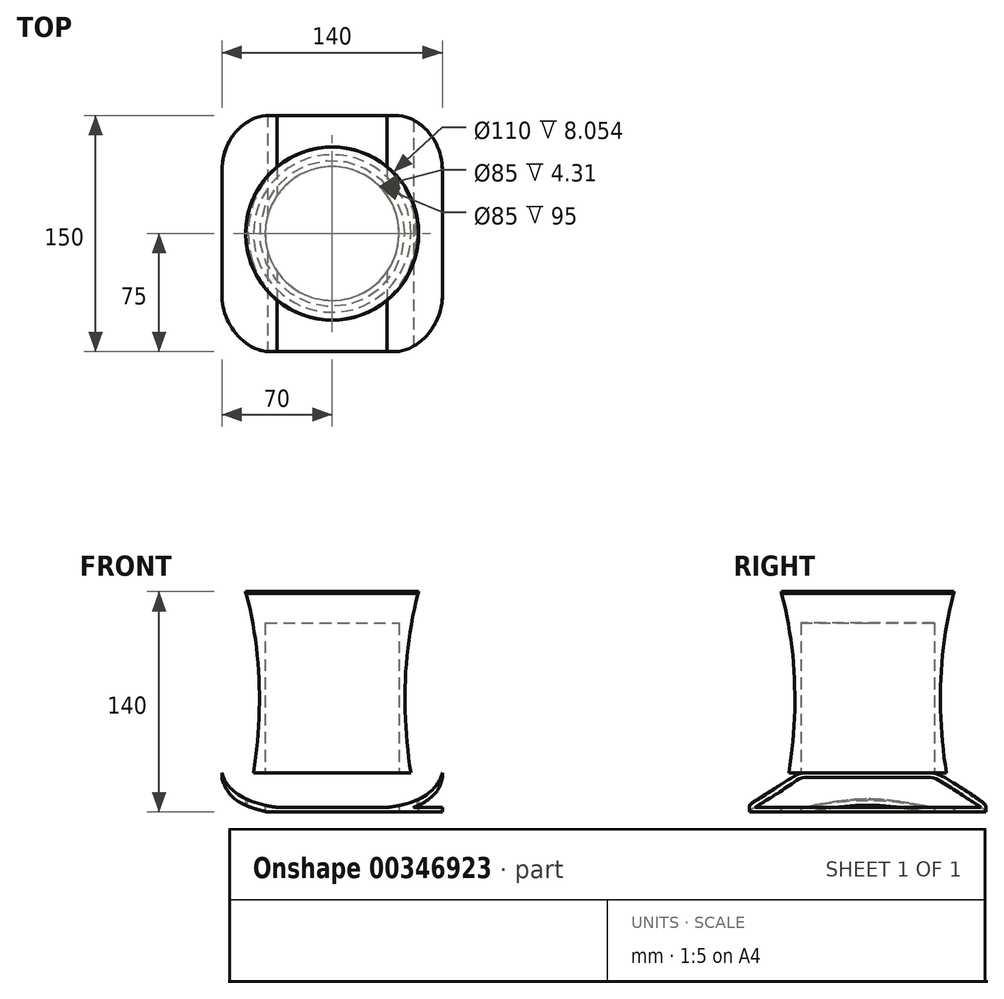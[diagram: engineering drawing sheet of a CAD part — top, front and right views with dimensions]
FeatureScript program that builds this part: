
annotation { "Feature Type Name" : "Feature", "Feature Type Description" : "" }
export const myFeature = defineFeature(function(context is Context, id is Id, definition is map)
    precondition{}
    {
        {
            var Q0;
            Q0=qCreatedBy(makeId("Top.planeOp"),FACE);
            var sketch = newSketch(context, id + "F0", { "sketchPlane" : qUnion([Q0])});
            skCircle(sketch, "E0", {"center": v(0, 0) * mm, "radius": 55 * mm});
            skSolve(sketch);
        }
        {
            var Q0;
            Q0=makeQuery(id+"F0.imprint","IMPRINT",FACE,{"disambiguationData":[TD([[makeQuery(id+"F0.imprint","IMPRINT",EDGE,{"derivedFrom":sQuery(id+"F0.wireOp",EDGE,"E0")}),1.0]])]});
            extrude(context, id + "F1", {"entities" : qUnion([Q0]), "depth" : 140 * mm});
        }
        {
            var Q0;
            Q0=makeQuery(id+"F1.opExtrude","CAP_FACE",FACE,{"disambiguationData":[OSD([sQuery(id+"F0.wireOp",EDGE,"E0")])],"isStart":true});
            var sketch = newSketch(context, id + "F2", { "sketchPlane" : qUnion([Q0])});
            skCircle(sketch, "E1", {"center": v(0, 0) * mm, "radius": 42.5 * mm});
            skSolve(sketch);
        }
        {
            var Q0;
            Q0=makeQuery(id+"F2.imprint","IMPRINT",FACE,{"disambiguationData":[TD([[makeQuery(id+"F2.imprint","IMPRINT",EDGE,{"derivedFrom":sQuery(id+"F2.wireOp",EDGE,"E1")}),1.0]])]});
            extrude(context, id + "F3", {"entities" : qUnion([Q0]), "operationType" : NewBodyOperationType.REMOVE, "oppositeDirection" : true, "depth" : 120 * mm});
        }
        {
            var Q0;
            Q0=qCreatedBy(makeId("Front.planeOp"),FACE);
            var sketch = newSketch(context, id + "F4", { "sketchPlane" : qUnion([Q0])});
            skFitSpline(sketch, "E2", {"points": [v(-54.88, 139.91) * mm, v(-55.14, 0) * mm], "startDerivative": vector(37.45, -140.44) * mm, "endDerivative": vector(-32.77, -131.05) * mm});
            skLineSegment(sketch, "E3", {"start": v(-54.88, 139.91) * mm, "end": v(-55.14, 0) * mm});
            skSolve(sketch);
        }
        {
            var Q0;
            Q0=makeQuery(id+"F4.imprint","IMPRINT",FACE,{"disambiguationData":[TD([[makeQuery(id+"F4.imprint","IMPRINT",EDGE,{"derivedFrom":sQuery(id+"F4.wireOp",EDGE,"E2")}),-1.0]])]});
            var Q1;
            Q1=makeQuery(id+"F1.opExtrude","CAP_EDGE",EDGE,{"disambiguationData":[OSD([sQuery(id+"F0.wireOp",EDGE,"E0")])],"isStart":true});
            revolve(context, id + "F5", {"operationType" : NewBodyOperationType.REMOVE, "entities" : qUnion([Q0]), "axis" : qUnion([Q1]), "revolveType" : RevolveType.FULL, "oppositeDirection" : true});
        }
        {
            var Q0;
            Q0=qCreatedBy(makeId("Front.planeOp"),FACE);
            var sketch = newSketch(context, id + "F6", { "sketchPlane" : qUnion([Q0])});
            skLineSegment(sketch, "E4.bottom", {"start": v(-55.94, 142.28) * mm, "end": v(-54.88, 142.28) * mm});
            skLineSegment(sketch, "E4.top", {"start": v(-55.94, 72.28) * mm, "end": v(-54.88, 72.28) * mm});
            skLineSegment(sketch, "E4.left", {"start": v(-55.94, 142.28) * mm, "end": v(-55.94, 72.28) * mm});
            skLineSegment(sketch, "E4.right", {"start": v(-54.88, 142.28) * mm, "end": v(-54.88, 72.28) * mm});
            skSolve(sketch);
        }
        {
            var Q0;
            Q0=makeQuery(id+"F6.imprint","IMPRINT",FACE,{"disambiguationData":[TD([[makeQuery(id+"F6.imprint","IMPRINT",EDGE,{"derivedFrom":sQuery(id+"F6.wireOp",EDGE,"E4.bottom")}),-1.0]])]});
            var Q1;
            Q1=makeQuery(id+"F1.opExtrude","CAP_EDGE",EDGE,{"disambiguationData":[OSD([sQuery(id+"F0.wireOp",EDGE,"E0")])],"isStart":false});
            revolve(context, id + "F7", {"operationType" : NewBodyOperationType.REMOVE, "entities" : qUnion([Q0]), "axis" : qUnion([Q1]), "revolveType" : RevolveType.FULL, "oppositeDirection" : true});
        }
        {
            var Q0;
            Q0=qCreatedBy(makeId("Top.planeOp"),FACE);
            var sketch = newSketch(context, id + "F8", { "sketchPlane" : qUnion([Q0])});
            skCircle(sketch, "E5", {"center": v(0, 0) * mm, "radius": 55 * mm});
            skLineSegment(sketch, "E6.bottom", {"start": v(0, 0) * mm, "end": v(70, 0) * mm});
            skLineSegment(sketch, "E6.top", {"start": v(0, 75) * mm, "end": v(70, 75) * mm});
            skLineSegment(sketch, "E6.left", {"start": v(0, 0) * mm, "end": v(0, 75) * mm});
            skLineSegment(sketch, "E6.right", {"start": v(70, 0) * mm, "end": v(70, 75) * mm});
            skLineSegment(sketch, "E7.bottom", {"start": v(0, 0) * mm, "end": v(-70, 0) * mm});
            skLineSegment(sketch, "E7.top", {"start": v(0, 75) * mm, "end": v(-70, 75) * mm});
            skLineSegment(sketch, "E7.right", {"start": v(-70, 0) * mm, "end": v(-70, 75) * mm});
            skLineSegment(sketch, "E8.top", {"start": v(0, -75) * mm, "end": v(70, -75) * mm});
            skLineSegment(sketch, "E8.left", {"start": v(0, 0) * mm, "end": v(0, -75) * mm});
            skLineSegment(sketch, "E8.right", {"start": v(70, 0) * mm, "end": v(70, -75) * mm});
            skLineSegment(sketch, "E9.top", {"start": v(0, -75) * mm, "end": v(-70, -75) * mm});
            skLineSegment(sketch, "E9.right", {"start": v(-70, 0) * mm, "end": v(-70, -75) * mm});
            skSolve(sketch);
        }
        {
            var Q0;
            {var subQ0=sQuery(id+"F8.wireOp",EDGE,"E8.top");Q0=makeQuery(id+"F8.imprint","IMPRINT",FACE,{"disambiguationData":[TD([[makeQuery(id+"F8.imprint","IMPRINT",EDGE,{"derivedFrom":subQ0}),1.0]])]});}
            var Q1;
            {var subQ1=sQuery(id+"F8.wireOp",EDGE,"E6.top");Q1=makeQuery(id+"F8.imprint","IMPRINT",FACE,{"disambiguationData":[TD([[makeQuery(id+"F8.imprint","IMPRINT",EDGE,{"derivedFrom":subQ1}),-1.0]])]});}
            var Q2;
            {var subQ1=sQuery(id+"F8.wireOp",EDGE,"E9.top");Q2=makeQuery(id+"F8.imprint","IMPRINT",FACE,{"disambiguationData":[TD([[makeQuery(id+"F8.imprint","IMPRINT",EDGE,{"derivedFrom":subQ1}),-1.0]])]});}
            var Q3;
            {var subQ2=sQuery(id+"F8.wireOp",EDGE,"E7.top");Q3=makeQuery(id+"F8.imprint","IMPRINT",FACE,{"disambiguationData":[TD([[makeQuery(id+"F8.imprint","IMPRINT",EDGE,{"derivedFrom":subQ2}),1.0]])]});}
            extrude(context, id + "F9", {"entities" : qUnion([Q0, Q1, Q2, Q3]), "operationType" : NewBodyOperationType.ADD, "depth" : 25 * mm});
        }
        {
            var Q0;
            Q0=makeQuery(id+"F9.opExtrude","CAP_FACE",FACE,{"disambiguationData":[OSD([sQuery(id+"F8.wireOp",EDGE,"E5"),sQuery(id+"F8.wireOp",EDGE,"E6.top"),sQuery(id+"F8.wireOp",EDGE,"E6.right"),sQuery(id+"F8.wireOp",EDGE,"E7.top"),sQuery(id+"F8.wireOp",EDGE,"E7.right"),sQuery(id+"F8.wireOp",EDGE,"E8.top"),sQuery(id+"F8.wireOp",EDGE,"E8.right"),sQuery(id+"F8.wireOp",EDGE,"E9.top"),sQuery(id+"F8.wireOp",EDGE,"E9.right")])],"isStart":false});
            var sketch = newSketch(context, id + "F10", { "sketchPlane" : qUnion([Q0])});
            skLineSegment(sketch, "E10", {"start": v(-70, 75) * mm, "end": v(-40, 75) * mm});
            skLineSegment(sketch, "E11", {"start": v(-70, 75) * mm, "end": v(-70, 40) * mm});
            skPoint(sketch, "E12", {"position": v(-70, 57.5) * mm});
            skFitSpline(sketch, "E13", {"points": [v(-40, 75) * mm, v(-70, 40) * mm], "startDerivative": vector(-45, 0) * mm, "endDerivative": vector(0, -61.02) * mm});
            skLineSegment(sketch, "E14", {"start": v(70, 75) * mm, "end": v(40, 75) * mm});
            skLineSegment(sketch, "E15", {"start": v(70, 75) * mm, "end": v(70, 40) * mm});
            skLineSegment(sketch, "E16", {"start": v(-70, -40) * mm, "end": v(-70, -75) * mm});
            skLineSegment(sketch, "E17", {"start": v(-70, -75) * mm, "end": v(-40, -75) * mm});
            skFitSpline(sketch, "E18", {"points": [v(-70, -40) * mm, v(-40, -75) * mm], "startDerivative": vector(0, -52.5) * mm, "endDerivative": vector(45, 0) * mm});
            skFitSpline(sketch, "E19", {"points": [v(40, 75) * mm, v(70, 40) * mm], "startDerivative": vector(45, 0) * mm, "endDerivative": vector(0, -60.24) * mm});
            skLineSegment(sketch, "E20", {"start": v(40, -75) * mm, "end": v(70, -75) * mm});
            skLineSegment(sketch, "E21", {"start": v(70, -75) * mm, "end": v(70, -40) * mm});
            skFitSpline(sketch, "E22", {"points": [v(40, -75) * mm, v(70, -40) * mm], "startDerivative": vector(45, 0) * mm, "endDerivative": vector(0, 52.5) * mm});
            skSolve(sketch);
        }
        {
            var Q0;
            Q0=makeQuery(id+"F10.imprint","IMPRINT",FACE,{"disambiguationData":[TD([[makeQuery(id+"F10.imprint","IMPRINT",EDGE,{"derivedFrom":sQuery(id+"F10.wireOp",EDGE,"E10")}),-1.0]])]});
            var Q1;
            Q1=makeQuery(id+"F10.imprint","IMPRINT",FACE,{"disambiguationData":[TD([[makeQuery(id+"F10.imprint","IMPRINT",EDGE,{"derivedFrom":sQuery(id+"F10.wireOp",EDGE,"E14")}),-1.0]])]});
            var Q2;
            Q2=makeQuery(id+"F10.imprint","IMPRINT",FACE,{"disambiguationData":[TD([[makeQuery(id+"F10.imprint","IMPRINT",EDGE,{"derivedFrom":sQuery(id+"F10.wireOp",EDGE,"E20")}),1.0]])]});
            var Q3;
            Q3=makeQuery(id+"F10.imprint","IMPRINT",FACE,{"disambiguationData":[TD([[makeQuery(id+"F10.imprint","IMPRINT",EDGE,{"derivedFrom":sQuery(id+"F10.wireOp",EDGE,"E16")}),1.0]])]});
            extrude(context, id + "F11", {"entities" : qUnion([Q0, Q1, Q2, Q3]), "operationType" : NewBodyOperationType.REMOVE, "oppositeDirection" : true, "depth" : 25 * mm});
        }
        {
            var Q0;
            Q0=makeQuery(id+"F9.opExtrude","SWEPT_FACE",FACE,{"disambiguationData":[OSD([sQuery(id+"F8.wireOp",EDGE,"E8.top"),sQuery(id+"F8.wireOp",EDGE,"E9.top")])]});
            var sketch = newSketch(context, id + "F12", { "sketchPlane" : qUnion([Q0])});
            skLineSegment(sketch, "E23", {"start": v(-70, 0) * mm, "end": v(-70, 3) * mm});
            skLineSegment(sketch, "E24", {"start": v(-70, 3) * mm, "end": v(70, 3) * mm});
            skLineSegment(sketch, "E25", {"start": v(70, 3) * mm, "end": v(35, 3) * mm});
            skLineSegment(sketch, "E26", {"start": v(-70, 3) * mm, "end": v(-35, 3) * mm});
            skFitSpline(sketch, "E27", {"points": [v(-70, 25) * mm, v(-35, 3) * mm], "startDerivative": vector(8.35, -38.78) * mm, "endDerivative": vector(47.93, -5.88) * mm});
            skFitSpline(sketch, "E28", {"points": [v(35, 3) * mm, v(70, 25) * mm], "startDerivative": vector(46.56, 4.95) * mm, "endDerivative": vector(11.27, 42.95) * mm});
            skLineSegment(sketch, "E29", {"start": v(70, 25) * mm, "end": v(70, 22) * mm});
            skLineSegment(sketch, "E30", {"start": v(35, 3) * mm, "end": v(41, 3) * mm});
            skLineSegment(sketch, "E31", {"start": v(-70, 25) * mm, "end": v(-70, 22) * mm});
            skLineSegment(sketch, "E32", {"start": v(-35, 3) * mm, "end": v(-41, 3) * mm});
            skPoint(sketch, "E33", {"position": v(-52.5, 3) * mm});
            skLineSegment(sketch, "E34", {"start": v(-70, 22) * mm, "end": v(-70, 3) * mm});
            skLineSegment(sketch, "E35", {"start": v(-70, 25) * mm, "end": v(0, 25) * mm});
            skLineSegment(sketch, "E36", {"start": v(0, 25) * mm, "end": v(0, 3) * mm});
            skLineSegment(sketch, "E37", {"start": v(0, 25) * mm, "end": v(70, 25) * mm});
            skLineSegment(sketch, "E38", {"start": v(70, 22) * mm, "end": v(70, 3) * mm});
            skLineSegment(sketch, "E39", {"start": v(41, 3) * mm, "end": v(41, 0) * mm});
            skFitSpline(sketch, "E40", {"points": [v(41, 0) * mm, v(70, 22) * mm], "startDerivative": vector(42.57, 9) * mm, "endDerivative": vector(6.7, 39.86) * mm});
            skLineSegment(sketch, "E41", {"start": v(-41, 3) * mm, "end": v(-41, 0) * mm});
            skFitSpline(sketch, "E42", {"points": [v(-70, 22) * mm, v(-41, 0) * mm], "startDerivative": vector(11.06, -49.07) * mm, "endDerivative": vector(34.5, -9) * mm});
            skLineSegment(sketch, "E43", {"start": v(-70, 0) * mm, "end": v(-41, 0) * mm});
            skLineSegment(sketch, "E44", {"start": v(70, 3) * mm, "end": v(70, 0) * mm});
            skLineSegment(sketch, "E45", {"start": v(70, 0) * mm, "end": v(41, 0) * mm});
            skSolve(sketch);
        }
        {
            var Q0;
            {var subQ0=sQuery(id+"F12.wireOp",EDGE,"E37");var subQ1=sQuery(id+"F12.wireOp",EDGE,"E28");var subQ2=makeQuery(id+"F12.imprint","INTERSECT",VERTEX,{"derivedFrom":[subQ1,sQuery(id+"F12.wireOp",EDGE,"E29"),subQ0]});Q0=makeQuery(id+"F12.imprint","IMPRINT",FACE,{"disambiguationData":[TD([[makeQuery(id+"F12.imprint","IMPRINT",EDGE,{"disambiguationData":[TD([[subQ2,1.0]])],"derivedFrom":subQ1}),1.0]])]});}
            var Q1;
            {var subQ0=sQuery(id+"F12.wireOp",EDGE,"E38");Q1=makeQuery(id+"F12.imprint","IMPRINT",FACE,{"disambiguationData":[TD([[makeQuery(id+"F12.imprint","IMPRINT",EDGE,{"derivedFrom":subQ0}),-1.0]])]});}
            var Q2;
            {var subQ3=sQuery(id+"F12.wireOp",EDGE,"E36");Q2=makeQuery(id+"F12.imprint","IMPRINT",FACE,{"disambiguationData":[TD([[makeQuery(id+"F12.imprint","IMPRINT",EDGE,{"derivedFrom":subQ3}),1.0]])]});}
            var Q3;
            {var subQ0=sQuery(id+"F12.wireOp",EDGE,"E36");Q3=makeQuery(id+"F12.imprint","IMPRINT",FACE,{"disambiguationData":[TD([[makeQuery(id+"F12.imprint","IMPRINT",EDGE,{"derivedFrom":subQ0}),-1.0]])]});}
            var Q4;
            {var subQ0=sQuery(id+"F12.wireOp",EDGE,"E35");var subQ1=sQuery(id+"F12.wireOp",EDGE,"E27");var subQ2=makeQuery(id+"F12.imprint","INTERSECT",VERTEX,{"derivedFrom":[subQ1,sQuery(id+"F12.wireOp",EDGE,"E31"),subQ0]});Q4=makeQuery(id+"F12.imprint","IMPRINT",FACE,{"disambiguationData":[TD([[makeQuery(id+"F12.imprint","IMPRINT",EDGE,{"disambiguationData":[TD([[subQ2,-1.0]])],"derivedFrom":subQ1}),1.0]])]});}
            var Q5;
            {var subQ0=sQuery(id+"F12.wireOp",EDGE,"E34");Q5=makeQuery(id+"F12.imprint","IMPRINT",FACE,{"disambiguationData":[TD([[makeQuery(id+"F12.imprint","IMPRINT",EDGE,{"derivedFrom":subQ0}),1.0]])]});}
            extrude(context, id + "F13", {"entities" : qUnion([Q0, Q1, Q2, Q3, Q4, Q5]), "operationType" : NewBodyOperationType.REMOVE, "depth" : 150 * mm});
        }
        {
            var Q0;
            Q0=makeQuery(id+"F2.imprint","IMPRINT",FACE,{"disambiguationData":[TD([[makeQuery(id+"F2.imprint","IMPRINT",EDGE,{"derivedFrom":sQuery(id+"F2.wireOp",EDGE,"E1")}),1.0]])]});
            extrude(context, id + "F14", {"entities" : qUnion([Q0]), "operationType" : NewBodyOperationType.REMOVE, "oppositeDirection" : true, "depth" : 50 * mm});
        }
        {
            var Q0;
            {var subQ0=sQuery(id+"F12.wireOp",EDGE,"E34");Q0=makeQuery(id+"F12.imprint","IMPRINT",FACE,{"disambiguationData":[TD([[makeQuery(id+"F12.imprint","IMPRINT",EDGE,{"derivedFrom":subQ0}),1.0]])]});}
            var Q1;
            {var subQ0=sQuery(id+"F12.wireOp",EDGE,"E23");Q1=makeQuery(id+"F12.imprint","IMPRINT",FACE,{"disambiguationData":[TD([[makeQuery(id+"F12.imprint","IMPRINT",EDGE,{"derivedFrom":subQ0}),1.0]])]});}
            var Q2;
            {var subQ0=sQuery(id+"F12.wireOp",EDGE,"E38");Q2=makeQuery(id+"F12.imprint","IMPRINT",FACE,{"disambiguationData":[TD([[makeQuery(id+"F12.imprint","IMPRINT",EDGE,{"derivedFrom":subQ0}),-1.0]])]});}
            var Q3;
            {var subQ0=sQuery(id+"F12.wireOp",EDGE,"E25");var subQ4=sQuery(id+"F12.wireOp",EDGE,"E40");var subQ5=makeQuery(id+"F12.imprint","INTERSECT",VERTEX,{"derivedFrom":[subQ0,subQ4]});Q3=makeQuery(id+"F12.imprint","IMPRINT",FACE,{"disambiguationData":[TD([[makeQuery(id+"F12.imprint","IMPRINT",EDGE,{"disambiguationData":[TD([[subQ5,1.0]])],"derivedFrom":subQ0}),1.0]])]});}
            extrude(context, id + "F15", {"entities" : qUnion([Q0, Q1, Q2, Q3]), "operationType" : NewBodyOperationType.REMOVE, "oppositeDirection" : true, "depth" : 150 * mm});
        }
        {
            var Q0;
            {var subQ0=sQuery(id+"F12.wireOp",EDGE,"E35");var subQ1=sQuery(id+"F12.wireOp",EDGE,"E27");var subQ2=makeQuery(id+"F12.imprint","INTERSECT",VERTEX,{"derivedFrom":[subQ1,sQuery(id+"F12.wireOp",EDGE,"E31"),subQ0]});Q0=makeQuery(id+"F12.imprint","IMPRINT",FACE,{"disambiguationData":[TD([[makeQuery(id+"F12.imprint","IMPRINT",EDGE,{"disambiguationData":[TD([[subQ2,-1.0]])],"derivedFrom":subQ1}),1.0]])]});}
            var Q1;
            {var subQ0=sQuery(id+"F12.wireOp",EDGE,"E36");Q1=makeQuery(id+"F12.imprint","IMPRINT",FACE,{"disambiguationData":[TD([[makeQuery(id+"F12.imprint","IMPRINT",EDGE,{"derivedFrom":subQ0}),-1.0]])]});}
            var Q2;
            {var subQ3=sQuery(id+"F12.wireOp",EDGE,"E36");Q2=makeQuery(id+"F12.imprint","IMPRINT",FACE,{"disambiguationData":[TD([[makeQuery(id+"F12.imprint","IMPRINT",EDGE,{"derivedFrom":subQ3}),1.0]])]});}
            var Q3;
            {var subQ0=sQuery(id+"F12.wireOp",EDGE,"E37");var subQ1=sQuery(id+"F12.wireOp",EDGE,"E28");var subQ2=makeQuery(id+"F12.imprint","INTERSECT",VERTEX,{"derivedFrom":[subQ1,sQuery(id+"F12.wireOp",EDGE,"E29"),subQ0]});Q3=makeQuery(id+"F12.imprint","IMPRINT",FACE,{"disambiguationData":[TD([[makeQuery(id+"F12.imprint","IMPRINT",EDGE,{"disambiguationData":[TD([[subQ2,1.0]])],"derivedFrom":subQ1}),1.0]])]});}
            extrude(context, id + "F16", {"entities" : qUnion([Q0, Q1, Q2, Q3]), "operationType" : NewBodyOperationType.REMOVE, "oppositeDirection" : true, "depth" : 150 * mm});
        }
        {
            var Q0;
            {var subQ0=sQuery(id+"F12.wireOp",EDGE,"E23");Q0=makeQuery(id+"F12.imprint","IMPRINT",FACE,{"disambiguationData":[TD([[makeQuery(id+"F12.imprint","IMPRINT",EDGE,{"derivedFrom":subQ0}),-1.0]])]});}
            extrude(context, id + "F17", {"entities" : qUnion([Q0]), "operationType" : NewBodyOperationType.REMOVE, "oppositeDirection" : true, "depth" : 150 * mm});
        }
    });
